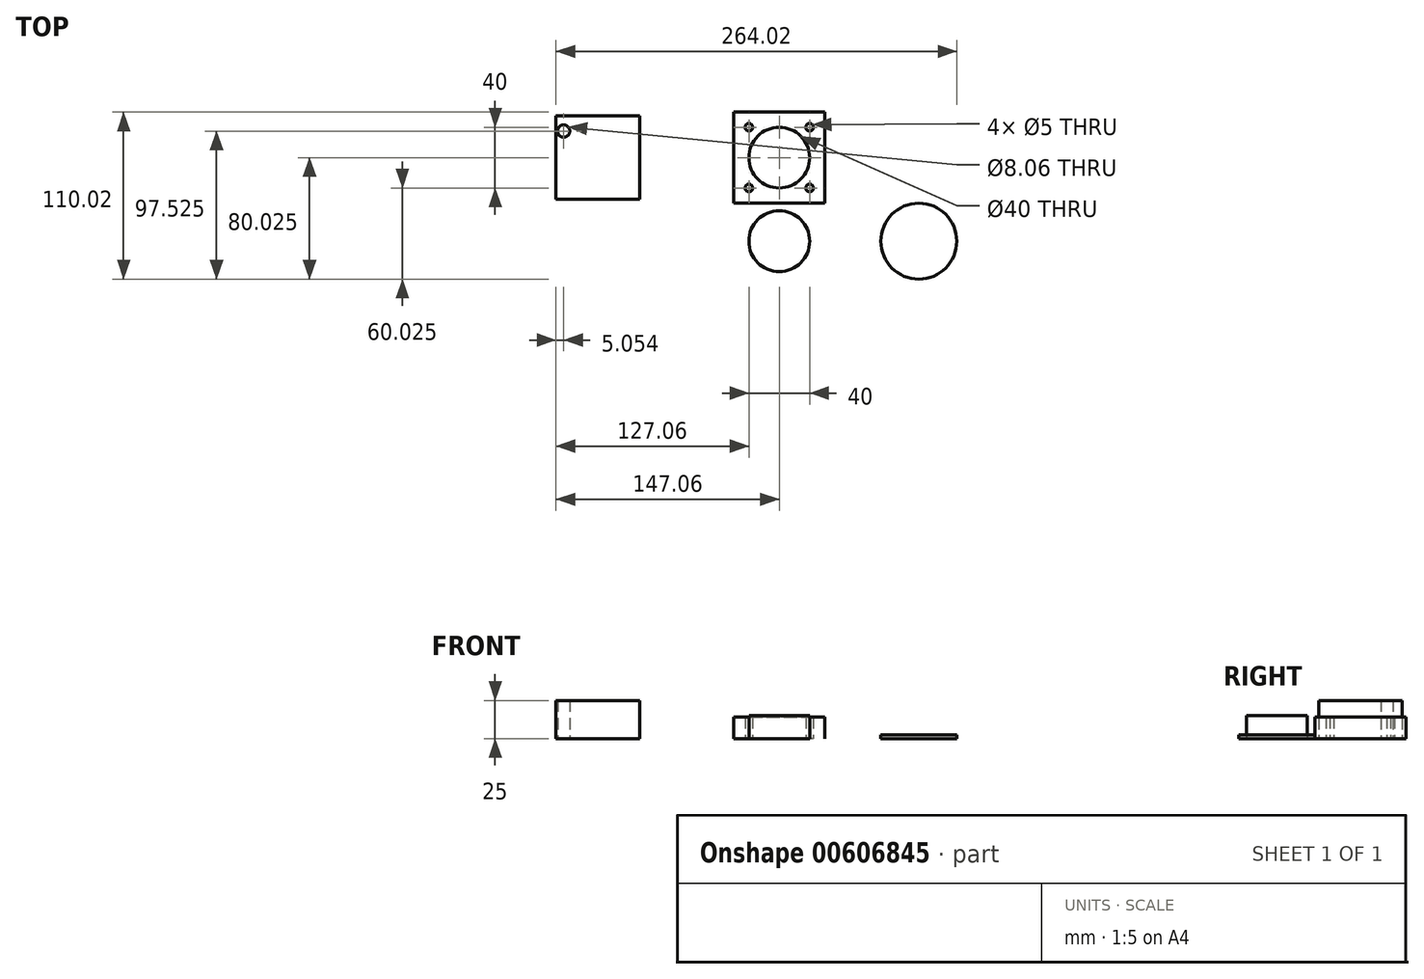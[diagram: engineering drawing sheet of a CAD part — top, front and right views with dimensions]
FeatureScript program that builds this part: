
annotation { "Feature Type Name" : "Feature", "Feature Type Description" : "" }
export const myFeature = defineFeature(function(context is Context, id is Id, definition is map)
    precondition{}
    {
        {
            var Q0;
            Q0=qCreatedBy(makeId("Top.planeOp"),FACE);
            var sketch = newSketch(context, id + "F0", { "sketchPlane" : qUnion([Q0])});
            skCircle(sketch, "E0", {"center": v(0, 0) * mm, "radius": 20 * mm});
            skLineSegment(sketch, "E1.bottom", {"start": v(-22.5, -34.39) * mm, "end": v(22.5, -34.39) * mm});
            skLineSegment(sketch, "E1.top", {"start": v(-22.5, -79.39) * mm, "end": v(22.5, -79.39) * mm});
            skLineSegment(sketch, "E1.left", {"start": v(-22.5, -34.39) * mm, "end": v(-22.5, -79.39) * mm});
            skLineSegment(sketch, "E1.right", {"start": v(22.5, -34.39) * mm, "end": v(22.5, -79.39) * mm});
            skPoint(sketch, "E1.middle", {"position": v(0, -56.89) * mm});
            skCircle(sketch, "E2", {"center": v(91.96, 0) * mm, "radius": 25 * mm});
            skLineSegment(sketch, "E3.bottom", {"start": v(-30, 85.02) * mm, "end": v(30, 85.02) * mm});
            skLineSegment(sketch, "E3.top", {"start": v(-30, 25.02) * mm, "end": v(30, 25.02) * mm});
            skLineSegment(sketch, "E3.left", {"start": v(-30, 85.02) * mm, "end": v(-30, 25.02) * mm});
            skLineSegment(sketch, "E3.right", {"start": v(30, 85.02) * mm, "end": v(30, 25.02) * mm});
            skPoint(sketch, "E3.middle", {"position": v(0, 55.02) * mm});
            skCircle(sketch, "E4", {"center": v(0, 55.02) * mm, "radius": 20 * mm});
            skLineSegment(sketch, "E5.bottom", {"start": v(-147.06, 82.52) * mm, "end": v(-92.06, 82.52) * mm});
            skLineSegment(sketch, "E5.top", {"start": v(-147.06, 27.52) * mm, "end": v(-92.06, 27.52) * mm});
            skLineSegment(sketch, "E5.left", {"start": v(-147.06, 82.52) * mm, "end": v(-147.06, 27.52) * mm});
            skLineSegment(sketch, "E5.right", {"start": v(-92.06, 82.52) * mm, "end": v(-92.06, 27.52) * mm});
            skPoint(sketch, "E5.middle", {"position": v(-119.56, 55.02) * mm});
            skCircle(sketch, "E6", {"center": v(-20, 75.02) * mm, "radius": 2.5 * mm});
            skCircle(sketch, "E7.MirrorC", {"center": v(20, 75.02) * mm, "radius": 2.5 * mm});
            skLineSegment(sketch, "E8", {"start": v(-20, 55.02) * mm, "end": v(0, 55.02) * mm, "construction": true});
            skCircle(sketch, "E9.MirrorC", {"center": v(-20, 35.02) * mm, "radius": 2.5 * mm});
            skCircle(sketch, "E10.MirrorC", {"center": v(20, 35.02) * mm, "radius": 2.5 * mm});
            skCircle(sketch, "E11", {"center": v(-142, 72.52) * mm, "radius": 4.03 * mm});
            skSolve(sketch);
        }
        {
            var Q0;
            Q0=makeQuery(id+"F0.imprint","IMPRINT",FACE,{"disambiguationData":[TD([[makeQuery(id+"F0.imprint","IMPRINT",EDGE,{"derivedFrom":sQuery(id+"F0.wireOp",EDGE,"E0")}),1.0]])]});
            extrude(context, id + "F1", {"entities" : qUnion([Q0]), "depth" : 15 * mm, "offsetDistance" : 25 * mm});
        }
        {
            var Q0;
            Q0=makeQuery(id+"F0.imprint","IMPRINT",FACE,{"disambiguationData":[TD([[makeQuery(id+"F0.imprint","IMPRINT",EDGE,{"derivedFrom":sQuery(id+"F0.wireOp",EDGE,"E3.bottom")}),-1.0]])]});
            extrude(context, id + "F2", {"entities" : qUnion([Q0]), "depth" : 14 * mm, "offsetDistance" : 25 * mm});
        }
        {
            var Q0;
            Q0=makeQuery(id+"F0.imprint","IMPRINT",FACE,{"disambiguationData":[TD([[makeQuery(id+"F0.imprint","IMPRINT",EDGE,{"derivedFrom":sQuery(id+"F0.wireOp",EDGE,"E2")}),1.0]])]});
            extrude(context, id + "F3", {"entities" : qUnion([Q0]), "depth" : 2.5 * mm, "offsetDistance" : 25 * mm});
        }
        {
            var Q0;
            Q0=makeQuery(id+"F0.imprint","IMPRINT",FACE,{"disambiguationData":[TD([[makeQuery(id+"F0.imprint","IMPRINT",EDGE,{"derivedFrom":sQuery(id+"F0.wireOp",EDGE,"E5.bottom")}),-1.0]])]});
            extrude(context, id + "F4", {"entities" : qUnion([Q0]), "depth" : 25 * mm, "offsetDistance" : 25 * mm});
        }
    });
